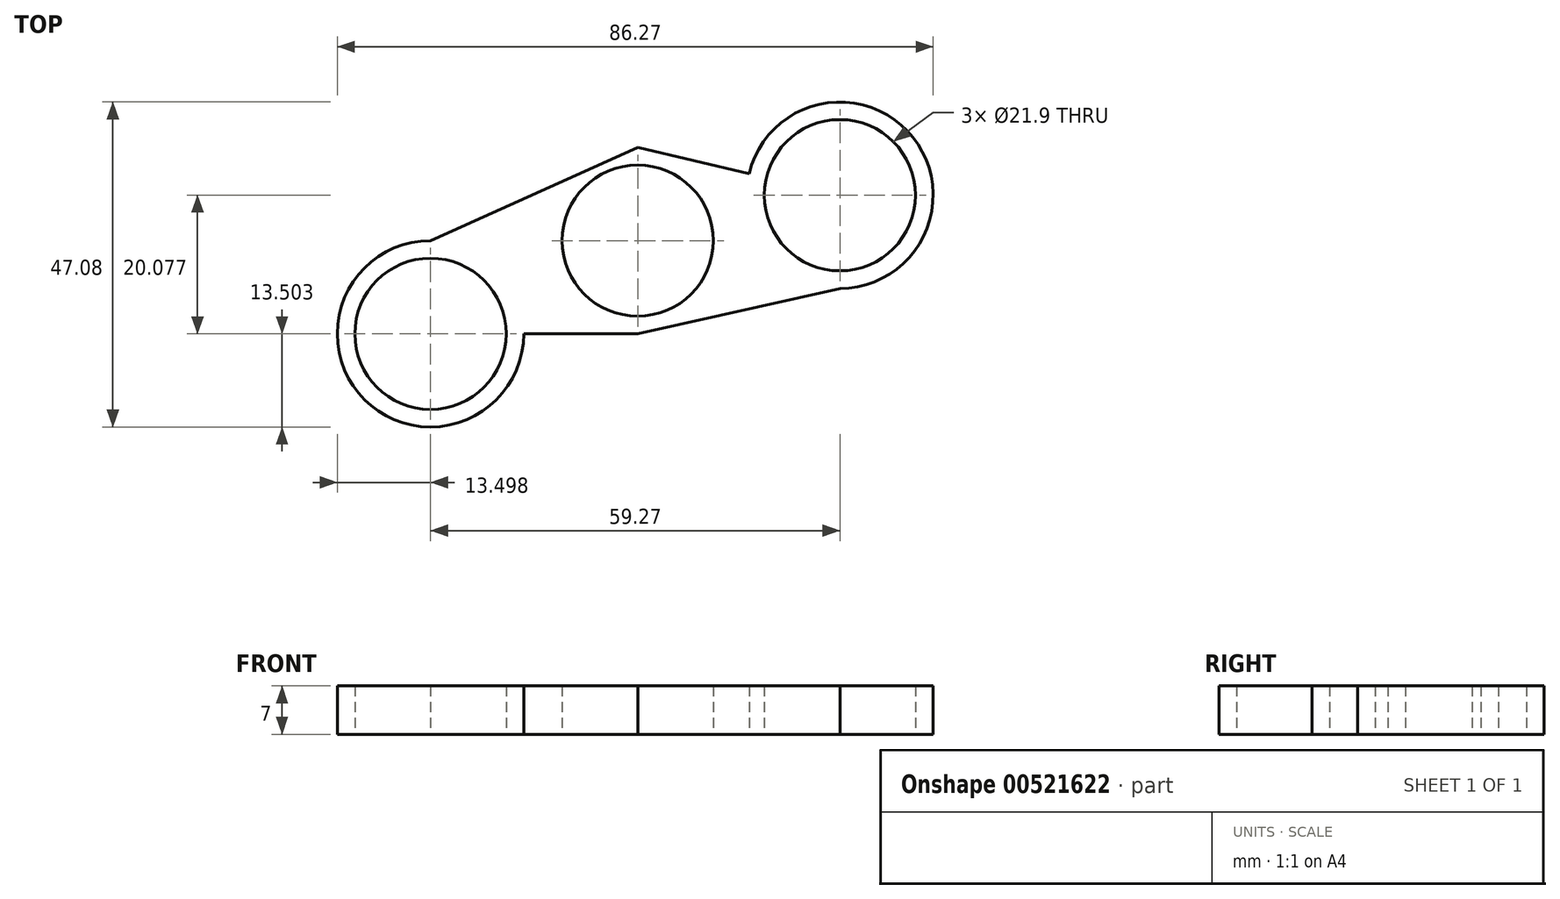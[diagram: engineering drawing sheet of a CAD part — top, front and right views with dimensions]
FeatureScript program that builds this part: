
annotation { "Feature Type Name" : "Feature", "Feature Type Description" : "" }
export const myFeature = defineFeature(function(context is Context, id is Id, definition is map)
    precondition{}
    {
        {
            var Q0;
            Q0=qCreatedBy(makeId("Top.planeOp"),FACE);
            var sketch = newSketch(context, id + "F0", { "sketchPlane" : qUnion([Q0])});
            skCircle(sketch, "E0", {"center": v(-26.2, 7.2) * mm, "radius": 13.5 * mm});
            skLineSegment(sketch, "E1", {"start": v(-26.2, -6.3) * mm, "end": v(-56.2, -6.3) * mm});
            skLineSegment(sketch, "E2", {"start": v(-26.2, 20.7) * mm, "end": v(3.08, 13.78) * mm});
            skCircle(sketch, "E3", {"center": v(-56.2, -6.3) * mm, "radius": 13.5 * mm});
            skCircle(sketch, "E4", {"center": v(3.08, 13.78) * mm, "radius": 13.5 * mm});
            skLineSegment(sketch, "E5", {"start": v(-26.2, 20.7) * mm, "end": v(-56.2, 7.2) * mm});
            skLineSegment(sketch, "E6", {"start": v(-26.2, -6.3) * mm, "end": v(3.08, 0.28) * mm});
            skCircle(sketch, "E7", {"center": v(-56.2, -6.3) * mm, "radius": 10.95 * mm});
            skCircle(sketch, "E8", {"center": v(-26.2, 7.2) * mm, "radius": 10.95 * mm});
            skCircle(sketch, "E9", {"center": v(3.08, 13.78) * mm, "radius": 10.95 * mm});
            skSolve(sketch);
        }
        {
            var Q0;
            Q0=makeQuery(id+"F0.imprint","IMPRINT",FACE,{"disambiguationData":[TD([[makeQuery(id+"F0.imprint","IMPRINT",EDGE,{"derivedFrom":sQuery(id+"F0.wireOp",EDGE,"OCI10V4E-xmeb-6PG1-i9MH-3baIQQBEKtpH")}),-1.0]])]});
            var Q1;
            Q1=makeQuery(id+"F0.imprint","IMPRINT",FACE,{"disambiguationData":[TD([[makeQuery(id+"F0.imprint","IMPRINT",EDGE,{"derivedFrom":sQuery(id+"F0.wireOp",EDGE,"ZuuP4U0j-2sd7-DQQf-FmC1-G0Gd94ltZZ03")}),-1.0]])]});
            var Q2;
            Q2=makeQuery(id+"F0.imprint","IMPRINT",FACE,{"disambiguationData":[TD([[makeQuery(id+"F0.imprint","IMPRINT",EDGE,{"derivedFrom":sQuery(id+"F0.wireOp",EDGE,"SZjJKZRk-D6kT-BvMT-yAbo-QVK3zUhes6C3")}),-1.0]])]});
            var Q3;
            {var subQ0=sQuery(id+"F0.wireOp",EDGE,"RGWL9e4D-vgDk-7Ye6-z0tZ-fzxPULNSaby1");var subQ1=sQuery(id+"F0.wireOp",EDGE,"b9Ac5Pd8-Vvi3-VtmM-CEAT-rNCfq9P8FT0j");var subQ2=makeQuery(id+"F0.imprint","INTERSECT",VERTEX,{"disambiguationData":[OD(0.0)],"derivedFrom":[subQ1,subQ0]});Q3=makeQuery(id+"F0.imprint","IMPRINT",FACE,{"disambiguationData":[TD([[makeQuery(id+"F0.imprint","IMPRINT",EDGE,{"disambiguationData":[TD([[subQ2,1.0]])],"derivedFrom":subQ1}),1.0]])]});}
            var Q4;
            {var subQ0=sQuery(id+"F0.wireOp",EDGE,"b9Ac5Pd8-Vvi3-VtmM-CEAT-rNCfq9P8FT0j");var subQ1=sQuery(id+"F0.wireOp",EDGE,"lfn33ZuF-LoLr-qM09-KkBq-lEixku48gx03");var subQ2=makeQuery(id+"F0.imprint","INTERSECT",VERTEX,{"disambiguationData":[OD(0.0)],"derivedFrom":[subQ1,subQ0]});Q4=makeQuery(id+"F0.imprint","IMPRINT",FACE,{"disambiguationData":[TD([[makeQuery(id+"F0.imprint","IMPRINT",EDGE,{"disambiguationData":[TD([[subQ2,1.0]])],"derivedFrom":subQ1}),1.0]])]});}
            var Q5;
            {var subQ0=sQuery(id+"F0.wireOp",EDGE,"6A3XPaUK-6yf9-frnd-pVEP-Y3nwWB9jF9C0");var subQ1=sQuery(id+"F0.wireOp",EDGE,"lfn33ZuF-LoLr-qM09-KkBq-lEixku48gx03");var subQ2=makeQuery(id+"F0.imprint","INTERSECT",VERTEX,{"disambiguationData":[OD(1.0)],"derivedFrom":[subQ1,subQ0]});Q5=makeQuery(id+"F0.imprint","IMPRINT",FACE,{"disambiguationData":[TD([[makeQuery(id+"F0.imprint","IMPRINT",EDGE,{"disambiguationData":[TD([[subQ2,-1.0]])],"derivedFrom":subQ1}),-1.0]])]});}
            var Q6;
            {var subQ0=sQuery(id+"F0.wireOp",EDGE,"jb3DJQSH-55Rq-jY2A-wEvF-ZN2afjJawSUB");var subQ1=sQuery(id+"F0.wireOp",EDGE,"lfn33ZuF-LoLr-qM09-KkBq-lEixku48gx03");var subQ2=makeQuery(id+"F0.imprint","INTERSECT",VERTEX,{"disambiguationData":[OD(1.0)],"derivedFrom":[subQ1,subQ0]});Q6=makeQuery(id+"F0.imprint","IMPRINT",FACE,{"disambiguationData":[TD([[makeQuery(id+"F0.imprint","IMPRINT",EDGE,{"disambiguationData":[TD([[subQ2,1.0]])],"derivedFrom":subQ1}),-1.0]])]});}
            var Q7;
            {var subQ0=sQuery(id+"F0.wireOp",EDGE,"633OGfyK-JdVI-E8w3-DHM4-iW958y6MR7CS");var subQ1=sQuery(id+"F0.wireOp",EDGE,"b9Ac5Pd8-Vvi3-VtmM-CEAT-rNCfq9P8FT0j");var subQ2=makeQuery(id+"F0.imprint","INTERSECT",VERTEX,{"derivedFrom":[subQ1,subQ0]});Q7=makeQuery(id+"F0.imprint","IMPRINT",FACE,{"disambiguationData":[TD([[makeQuery(id+"F0.imprint","IMPRINT",EDGE,{"disambiguationData":[TD([[subQ2,1.0]])],"derivedFrom":subQ1}),-1.0]])]});}
            var Q8;
            {var subQ0=sQuery(id+"F0.wireOp",EDGE,"V9QtUkcZ-tXAm-pJFA-mARk-y8nBa68ZiNzr");var subQ1=sQuery(id+"F0.wireOp",EDGE,"b9Ac5Pd8-Vvi3-VtmM-CEAT-rNCfq9P8FT0j");var subQ2=makeQuery(id+"F0.imprint","INTERSECT",VERTEX,{"derivedFrom":[subQ1,subQ0]});Q8=makeQuery(id+"F0.imprint","IMPRINT",FACE,{"disambiguationData":[TD([[makeQuery(id+"F0.imprint","IMPRINT",EDGE,{"disambiguationData":[TD([[subQ2,-1.0]])],"derivedFrom":subQ1}),-1.0]])]});}
            var Q9;
            {var subQ0=sQuery(id+"F0.wireOp",EDGE,"E3");var subQ1=makeQuery(id+"F0.imprint","INTERSECT",VERTEX,{"derivedFrom":[subQ0,sQuery(id+"F0.wireOp",EDGE,"E5")]});Q9=makeQuery(id+"F0.imprint","IMPRINT",FACE,{"disambiguationData":[TD([[makeQuery(id+"F0.imprint","IMPRINT",EDGE,{"disambiguationData":[TD([[subQ1,1.0]])],"derivedFrom":subQ0}),1.0]])]});}
            var Q10;
            {var subQ3=sQuery(id+"F0.wireOp",EDGE,"E5");var subQ5=sQuery(id+"F0.wireOp",EDGE,"E3");var subQ7=makeQuery(id+"F0.imprint","INTERSECT",VERTEX,{"derivedFrom":[subQ5,subQ3]});Q10=makeQuery(id+"F0.imprint","IMPRINT",FACE,{"disambiguationData":[TD([[makeQuery(id+"F0.imprint","IMPRINT",EDGE,{"disambiguationData":[TD([[subQ7,1.0]])],"derivedFrom":subQ5}),-1.0]])]});}
            var Q11;
            {var subQ1=sQuery(id+"F0.wireOp",EDGE,"E2");var subQ2=sQuery(id+"F0.wireOp",EDGE,"E0");var subQ4=makeQuery(id+"F0.imprint","INTERSECT",VERTEX,{"derivedFrom":[subQ2,subQ1]});Q11=makeQuery(id+"F0.imprint","IMPRINT",FACE,{"disambiguationData":[TD([[makeQuery(id+"F0.imprint","IMPRINT",EDGE,{"disambiguationData":[TD([[subQ4,1.0]])],"derivedFrom":subQ2}),1.0]])]});}
            var Q12;
            {var subQ0=sQuery(id+"F0.wireOp",EDGE,"E2");var subQ1=sQuery(id+"F0.wireOp",EDGE,"E0");var subQ2=makeQuery(id+"F0.imprint","INTERSECT",VERTEX,{"derivedFrom":[subQ1,subQ0]});Q12=makeQuery(id+"F0.imprint","IMPRINT",FACE,{"disambiguationData":[TD([[makeQuery(id+"F0.imprint","IMPRINT",EDGE,{"disambiguationData":[TD([[subQ2,1.0]])],"derivedFrom":subQ1}),-1.0]])]});}
            var Q13;
            {var subQ0=sQuery(id+"F0.wireOp",EDGE,"E4");var subQ1=makeQuery(id+"F0.imprint","INTERSECT",VERTEX,{"derivedFrom":[subQ0,sQuery(id+"F0.wireOp",EDGE,"E6")]});Q13=makeQuery(id+"F0.imprint","IMPRINT",FACE,{"disambiguationData":[TD([[makeQuery(id+"F0.imprint","IMPRINT",EDGE,{"disambiguationData":[TD([[subQ1,1.0]])],"derivedFrom":subQ0}),1.0]])]});}
            extrude(context, id + "F1", {"entities" : qUnion([Q0, Q1, Q2, Q3, Q4, Q5, Q6, Q7, Q8, Q9, Q10, Q11, Q12, Q13]), "depth" : 7 * mm, "offsetDistance" : 25 * mm});
        }
    });
